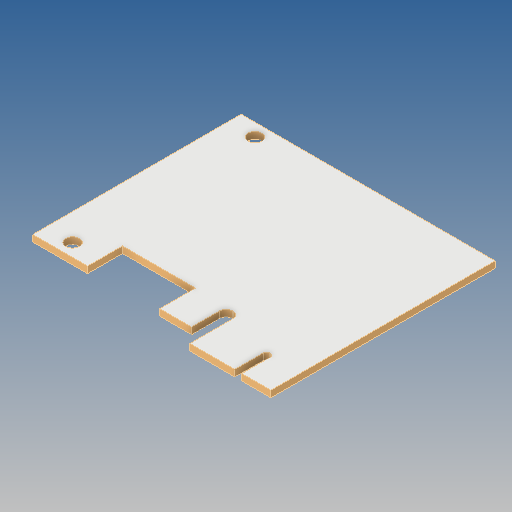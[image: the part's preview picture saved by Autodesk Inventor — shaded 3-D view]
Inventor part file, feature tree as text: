
AUTODESK INVENTOR PART (.ipt)
format: ipt  version: 2018 (Build 220112000, 112)  size: 101,376 bytes
history: native  units: mm
features: hole x1
ambient origin geometry x8: Origin, YZ Plane, XZ Plane, XY Plane, X Axis, Y Axis, Z Axis, Center Point
bodies: Solid1 (feature_tree)
feature tree (1):
  hole  "holes"  [1 undecoded]
note: 1 required parameter value undecoded (feature->parameter linkage not recoverable at this tier; creation-order binding heuristic only, values carry confidence <= 0.55)
